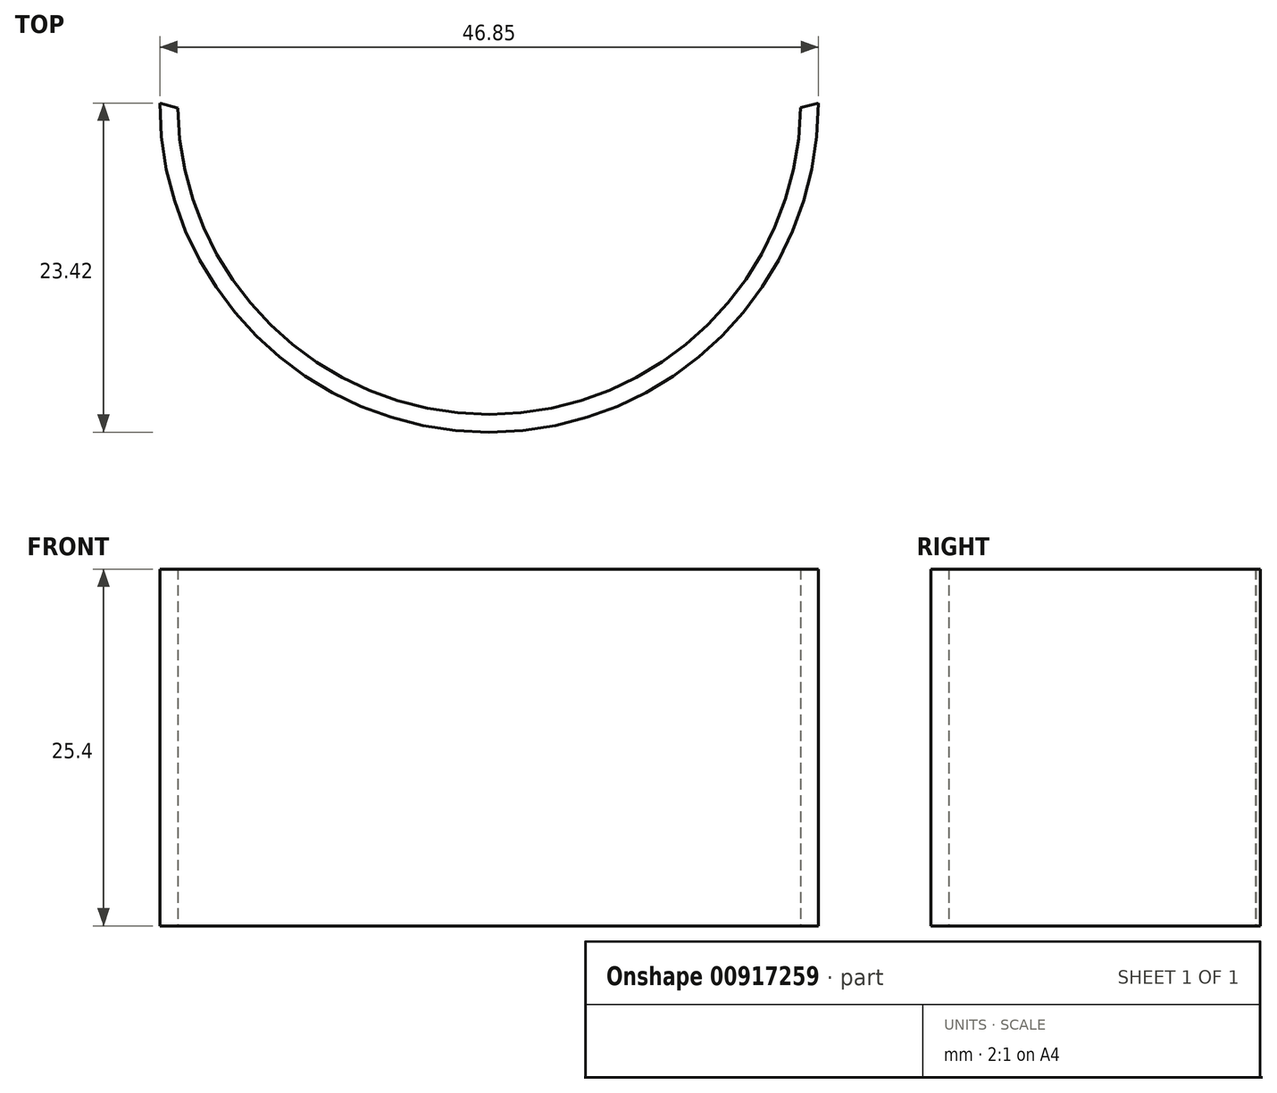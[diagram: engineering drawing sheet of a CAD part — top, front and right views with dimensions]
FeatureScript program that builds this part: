
annotation { "Feature Type Name" : "Feature", "Feature Type Description" : "" }
export const myFeature = defineFeature(function(context is Context, id is Id, definition is map)
    precondition{}
    {
        {
            var Q0;
            Q0=qCreatedBy(makeId("Top.planeOp"),FACE);
            var sketch = newSketch(context, id + "F0", { "sketchPlane" : qUnion([Q0])});
            skArc(sketch, "E0", {"start": v(-20.66, 0) * mm, "mid": v(2.76, -23.42) * mm, "end": v(26.19, 0) * mm});
            skArc(sketch, "E1.0", {"start": v(-19.4, -0.34) * mm, "mid": v(2.78, -22.15) * mm, "end": v(24.91, -0.31) * mm});
            skLineSegment(sketch, "E2", {"start": v(-20.66, 0) * mm, "end": v(-19.4, -0.34) * mm});
            skLineSegment(sketch, "E3", {"start": v(24.91, -0.31) * mm, "end": v(26.19, 0) * mm});
            skSolve(sketch);
        }
        {
            var Q0;
            Q0=makeQuery(id+"F0.imprint","IMPRINT",FACE,{"disambiguationData":[TD([[makeQuery(id+"F0.imprint","IMPRINT",EDGE,{"derivedFrom":sQuery(id+"F0.wireOp",EDGE,"E0")}),1.0]])]});
            extrude(context, id + "F1", {"entities" : qUnion([Q0]), "depth" : 25.4 * mm, "offsetDistance" : 25.4 * mm});
        }
    });
